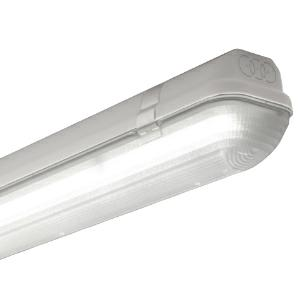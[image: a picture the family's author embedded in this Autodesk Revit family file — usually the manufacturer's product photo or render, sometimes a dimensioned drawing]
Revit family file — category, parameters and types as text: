
# Revit family: 3f_filippi_-_3f_linda_3f_filippi_-_58607_-_3f_linda_led_1x30w-830_l1570
name_source: partatom
category: Lighting Fixtures
units: mm (PartAtom-declared; Revit-internal decimal feet)

## family parameters
Cut with Voids When Loaded = No
Host = Face
Light Source = No
Part Type = Normal
Room Calculation Point = No
Round Connector Dimension = Use Diameter
Shared = No

## types (1)
- 3F Filippi - 3F Linda (1 x LED, 4921 lm, 33.5 W, 3000 K)
    Apparent Load = 34 VA
    Approval mark = CE
    CIE Flux Codes = 44 77 94 97 100
    Color Rendering = 80
    Color Temperature = 3000 K
    Control Gear = Electronic ballast
    Default Elevation = 1800 mm
    Description = ILLUMINOTECHNICAL
Luminous efficiency 100% (DLOR 97%, ULOR 3%).
Initial luminous flux of the luminaire 4921 lm.
Controlled symmetric distribution.
Installation Interdistance Transv.D = 1.77 x hu - Long.D = 1.17 x hu.
Tabular UGR (CIE 117 - 4H-8H; S=0.25H; 70/50/20): RUG 21.9 - 22.9.
Beam angle: 109° - 64°.
Luminous efficacy 147 lm/W.
Lifetime (L93/B10): 30000 h. (tq+25°C)
Lifetime (L90/B10): 50000 h. (tq+25°C)
Lifetime (L85/B10): 80000 h. (tq+25°C)
Lifetime (L80/B10): 100000 h. (tq+25°C)
Lifetime (L85/B10): 50000 h. (tq+35°C)
Sudden decreased luminous flux after 50000 hours: 0% (C0).
Photobiological safety in compliance with IEC/TR 62778: RG0 risk exempt, (IEC 62471).
In compliance with IEC/EN 62722-2-1 - IEC/EN 62717 standards.

SOURCE
Linear LED module 30W/830.
Energy efficiency class (UE 2019/2020 - UE 2019/2015): D.
CIE 13.3 Colour rendering index: CRI >80 (R9 <50%).
IES TM-30 Fidelity Index: Rf = 84 Rg = 95.
CCT nominal colour temperature 3000 K.
Colour initial tolerance (MacAdam): SDCM 3.

MECHANICAL
Self-extinguishing V2 polycarbonate housing, injection moulded, RAL 7035 grey.
Ecologic anti-aging injected sealing gasket.
Diffuser in self-extinguishing V2 polycarbonate, photo-engraved interior, UV stabilised, injection moulded with smooth outer surface, tamper-proof opening.
Gear-holder reflector in hot-dip galvanised steel, painted with white polyester base.
Snug fit safety snap-lock clips for diffuser mounting in stainless steel, screwdriver opening.
Fixing brackets in stainless steel.
Possibility for technicians to access the interior of the luminaire.
Luminaire with limited surface temperature. - D - (EN 60598-2-24)
Dimensions: 1570x100 mm, height 100 mm. Weight 2.5 kg.
IP66 protection degree.
Mechanical strength to impacts IK10 (20 joule).
Glow-wire test resistance 850°C.

ELECTRICAL
Halogen Free electronic wiring 230V-50/60Hz, power factor 0.90, THD <25%, constant output current, SELV, class I, 1 driver.
Power of the luminaire 33.5 W.
ENEC - CE.
SAFE FLICKER: PstLM=<1 and SVM=<0.4 (IEC TR 61547-1 and IEC TR 63158), to ensure a more comfortable and safe light.
Luminaire compliant with EN 60598-2-22 for power supply from a centralised emergency system CPSS (Central Power Supply System), not incorporated in the luminaire - high risk areas excluded. The default power and flux are 100% in AC and 100% in DC.
Ambient temperature from -20°C to +35°C.
Temperature class T6 max 85°C.
Relative humidity UR: <85%.

INSTALLATION
Ceiling / Suspended / Wall.
All accessories dedicated to this product are available on the Catalog and on our website www.3F-Filippi.com.

APPLICATIONS
Suitable product for food production plants (HACCP), IFS (Food Version 6), BRC (GSFS Food Version 7).
Dry, dusty indoor environments, subject to occasional water splashes.
Virtually shatterproof polycarbonate compatibly with the fumes / atmospheres that compromise the elasticity of plastic materials.
Not suitable for installation on surfaces subject to important vibrations, exposed to weather conditions, on ropes or poles.
Suitable for illumination of public car parks and parking grounds referred to DIN 67528:2018-04.

WARNING
Fixture not suitable for cold stores with an ambient temperature <0°C and/or relative humidity >85%.
Luminaire designed for disposal/recycling at end-of-life.
Replaceable (LED only) light source by a professional. Replaceable control gear by a professional.
    Height = 100 mm  [stored 0.328084 ft]
    Lamp = 1 x LED
    Lamp Light Flux = 4921 lm
    Lamp Power = 33.5 W
    Lamp count = 1
    Length = 1570 mm
    Lifetime = 50000 h
    Luminous efficacy = 147 lm/W
    Manufacturer = 3F Filippi
    ModVariant = No
    Model = 3F Filippi - 58607 - 3F Linda LED 1x30W-830 L1570
    Mounting Place = Ceiling
    Mounting Type = Pendant
    Number of Poles = 1
    OnlyDefault = Yes
    Power Factor = 1
    Product Name = 3F Filippi - 3F Linda
    Product group = pendant luminaire
    ProductGroupID = 9
    Protection Class = Protection class I
    Protection Degree = IP 66
    RLX_Detail_Level = 1
    RLX_Emergency_Light_Flux = 0 lm
    RLX_Emergency_Type = 0
    RLX_Emergency_Type_DB = No
    RlxData = <blob elided: 70729 chars, md5=8b90a34d>
    Socket = socket
    Standby Power = 0 W
    System Light Flux = 4921 lm
    System Power = 34 W
    Type Comments = Product without accessories
    Type Image = 3ffilippi_3f_linda_led.jpg
    URL = http://relux.com
    VarID = ---
    Voltage = 0 V
    Weight = 0.00 kg
    Width = 100 mm  [stored 0.328084 ft]

note: [stored X ft] marks values corroborated as IEEE doubles in the binary element streams (Revit-internal decimal feet)

## geometry (parser evidence)
native form markers: Blend x4, Sweep x8
no freeform markers — native parametric forms only
